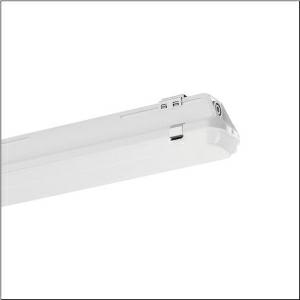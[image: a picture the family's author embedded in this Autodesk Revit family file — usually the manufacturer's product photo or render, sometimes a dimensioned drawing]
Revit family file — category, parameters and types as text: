
# Revit family: monsun_21_51fb10dp360c
name_source: partatom
category: Lighting Fixtures
units: mm (PartAtom-declared; Revit-internal decimal feet)

## family parameters
Cut with Voids When Loaded = No
Host = Face
Light Source = No
Part Type = Normal
Room Calculation Point = No
Round Connector Dimension = Use Diameter
Shared = No

## types (1)
- --- (1 x LED, 6060 lm, 34.9 W, 3000K)
    Apparent Load = 35 VA
    CIE Flux Codes = 47 77 93 94 100
    Color Rendering = 80
    Color Temperature = 3000K
    Default Elevation = 1800 mm
    Description = Monsun 21, damp-proof luminaire, chain hanger, primary optical cover: enclosure, of PMMA, light emission: direct distribution, primary light characteristic: symmetric, installation type: suspended mounting, surface-mounted, horizontal mounting, vertical mounting, LED, rated luminous flux: 6.060lm, luminous efficacy: 174lm/W, light colour: 830, colour temperature: 3000K, control gear: DALI 2, with terminal, 5-pole, max. 2.5mm², mains connection: 220..240V, AC, 50/60Hz, rated input power: 35W, housing, of glass-fibre reinforced polyester, uncoated, bright grey, incl. chain hanger, length: 1.590mm, width: 90mm, height: 88mm, clip for enclosure, of stainless steel (V2A), ceiling mounting element, of stainless steel (V2A), chain hanger, of stainless steel (V2A), protection rating (complete): IP66, insulation class (complete): insulation class I (protective earthing), certification: CE, ENEC, VDE, UKCA, protection symbol: D, impact resistance: IK04, permissible operating ambient temperature: -25..+35°C, standard: EN 50419, EN 60598-2-1, corresponds to IFS (International Featured Standards) requirements for safety and quality in the food industry, for indoor or canopied outdoor use, no direct snow, no direct sun, no direct rain, LABS conformity tested according to VDMA 24364:2018-05, contact your sales advisor before using the luminaires in applications with unclear chemical exposure, large temperature fluctuations or condensation-forming humidity, packaging unit: 1 piece
    Height = 89 mm
    Lamp = 1 x LED
    Lamp Light Flux = 6060 lm
    Lamp Power = 34.9 W
    Lamp count = 1
    Length = 1590 mm
    Luminous efficacy = 174 lm/W
    Manufacturer = Siteco
    ModVariant = No
    Model = 51FB10DP360C
    Mounting Place = Ceiling
    Mounting Type = Surface mounted
    Number of Poles = 1
    OnlyDefault = Yes
    Power Factor = 1
    Product Name = Monsun 21
    Product group = damp-proof luminaire
    ProductGroupID = 300
    Protection Class = Protection class I
    Protection Degree = IP 66
    RLX_Detail_Level = 1
    RLX_Emergency_Light_Flux = 0 lm
    RLX_Emergency_Type = 0
    RLX_Emergency_Type_DB = No
    RlxData = <blob elided: 92261 chars, md5=dae8de15>
    Socket = socket
    Standby Power = 0 W
    System Light Flux = 6060 lm
    System Power = 35 W
    Type Comments = factory setting: luminous flux: 100 % | dim-lin: 254 | 245 mA
    Type Image = l_1319656.jpg
    URL = http://relux.com
    VarID = @adj_038609
    Voltage = 0 V
    Weight = 0.00 kg
    Width = 90 mm

## geometry (parser evidence)
native form markers: Blend x4, Sweep x13
no freeform markers — native parametric forms only
